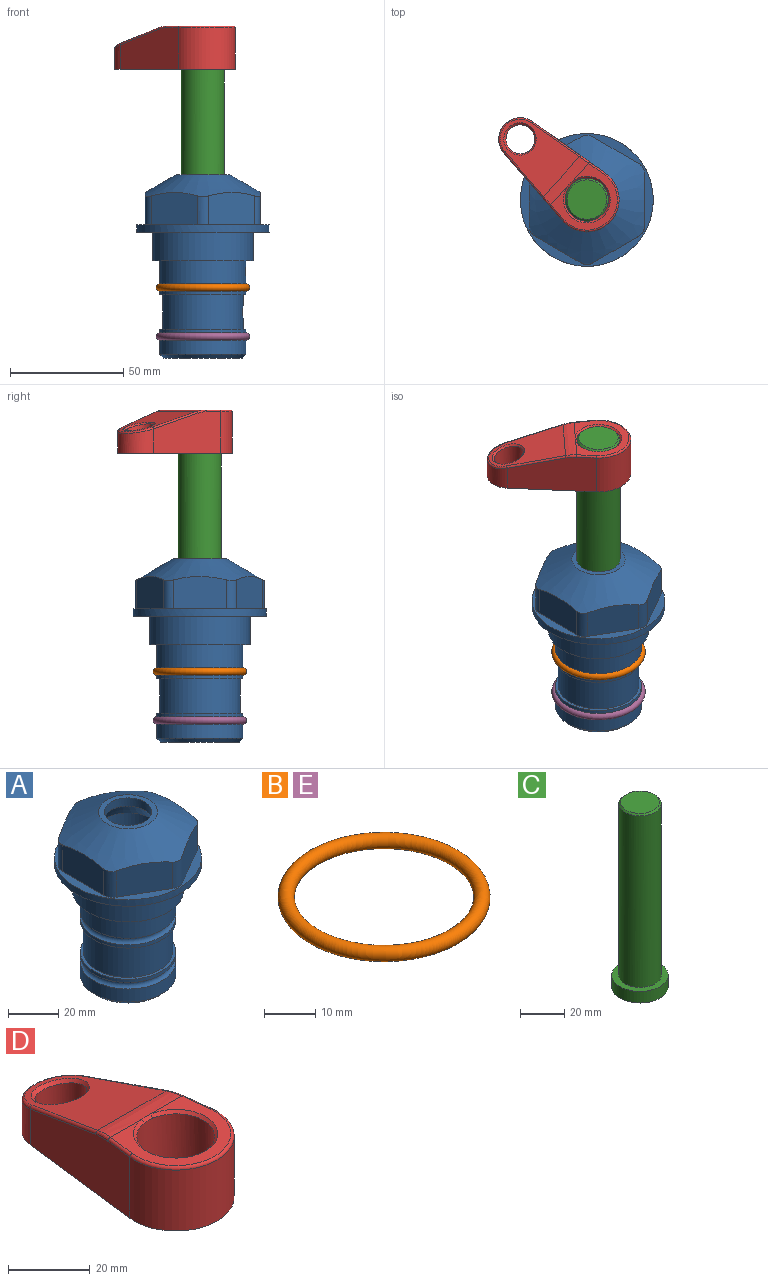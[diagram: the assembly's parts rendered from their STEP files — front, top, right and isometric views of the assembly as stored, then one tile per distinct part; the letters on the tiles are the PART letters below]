
ASSEMBLY  parts=5 mates=4
PART A: 36 faces, bbox 58.7x58.7x81 mm
  f0: cylinder r=17.78mm len=35.56mm, axis (0,0,1), area 1670.8mm2, adj f23,f24,f31
  f1: cylinder r=19.05mm len=38.1mm, axis (0,0,1), area 1191.9mm2, adj f26,f27,f30
  f2: plane 58.66x58.66mm, normal (0,0,-1), area 1150.6mm2, adj f3,f28
  f3: cylinder r=29.33mm len=58.66mm, axis (0,0,-1), area 585.1mm2, adj f2,f4
  f4: plane 58.66x58.66mm, normal (0,0,1), area 475.9mm2, adj f3,f5,f6,f7,f8,f9,f10,f11
  f5: plane 20.32x14.34mm, normal (-0.5,0.87,0), area 324.4mm2, adj f4,f15,f16,f17
  f6: plane 20.32x14.34mm, normal (0.5,0.87,0), area 324.4mm2, adj f4,f14,f15,f17
  f7: plane 23.48x14.34mm, normal (1,0,0), area 324.4mm2, adj f4,f13,f14,f17
  f8: plane 20.32x14.34mm, normal (0.5,-0.87,0), area 324.4mm2, adj f4,f12,f13,f17
  f9: plane 20.32x14.34mm, normal (-0.5,-0.87,0), area 324.4mm2, adj f4,f11,f12,f17
  f10: plane 23.48x14.34mm, normal (-1,0,0), area 324.4mm2, adj f4,f11,f16,f17
  f11: cylinder r=5.08mm len=12.85mm, axis (0,0,-1), area 67.2mm2, adj f4,f9,f10,f17
  f12: cylinder r=5.08mm len=12.85mm, axis (0,0,-1), area 67.2mm2, adj f4,f8,f9,f17
  f13: cylinder r=5.08mm len=12.85mm, axis (0,0,-1), area 67.2mm2, adj f4,f7,f8,f17
  f14: cylinder r=5.08mm len=12.85mm, axis (0,0,-1), area 67.2mm2, adj f4,f6,f7,f17
  f15: cylinder r=5.08mm len=12.85mm, axis (0,0,-1), area 67.2mm2, adj f4,f5,f6,f17
  f16: cylinder r=5.08mm len=12.85mm, axis (0,0,-1), area 67.2mm2, adj f4,f5,f10,f17
  f17: cone r=11.73mm half-angle=60deg, axis (0,0,-1), area 2071.8mm2, adj f5,f6,f7,f8,f9,f10,f11,f12
  f18: plane 23.46x23.46mm, normal (0,0,1), area 147.4mm2, adj f17,f35
  f19: plane 34.93x34.93mm, normal (0,0,-1), area 958mm2, adj f29
  f20: cylinder r=19.05mm len=38.1mm, axis (0,0,1), area 760.1mm2, adj f21,f29
  f21: torus R=19.05mm, axis (0,0,1), area 565.3mm2, adj f20,f22
  f22: cylinder r=19.05mm len=38.1mm, axis (0,0,1), area 190mm2, adj f21,f23
  f23: plane 38.1x38.1mm, normal (0,0,1), area 146.9mm2, adj f0,f22
  f24: plane 38.1x38.1mm, normal (0,0,-1), area 146.9mm2, adj f0,f25
  f25: cylinder r=19.05mm len=38.1mm, axis (0,0,1), area 190mm2, adj f24,f26
  f26: torus R=19.05mm, axis (0,0,1), area 565.3mm2, adj f1,f25
  f27: plane 44.45x44.45mm, normal (0,0,-1), area 411.7mm2, adj f1,f28
  f28: cylinder r=22.23mm len=44.45mm, axis (0,0,1), area 1773.5mm2, adj f2,f27
  f29: cone r=19.05mm half-angle=45deg, axis (0,0,1), area 257.5mm2, adj f19,f20
  f30: cylinder r=3.17mm len=6.75mm, axis (-1,0,0), area 128mm2, adj f1,f33
  f31: cylinder r=3.17mm len=6.35mm, axis (-1,0,0), area 102.5mm2, adj f0,f33
  f32: plane 25.4x25.4mm, normal (0,0,1), area 506.7mm2, adj f33
  f33: cylinder r=12.7mm len=66.42mm, axis (0,0,-1), area 5236.2mm2, adj f30,f31,f32,f34
  f34: cone r=9.53mm half-angle=30deg, axis (0,0,-1), area 443.4mm2, adj f33,f35
  f35: cylinder r=9.53mm len=19.05mm, axis (0,0,-1), area 240.9mm2, adj f18,f34
PART B: 1 faces, bbox 44.7x44.7x3.2 mm
  f0: torus R=19.05mm, axis (0,0,1), area 1193.9mm2
PART C: 6 faces, bbox 25.4x25.4x101.6 mm
  f0: plane 17.46x17.46mm, normal (0,0,1), area 239.5mm2, adj f5
  f1: plane 25.4x25.4mm, normal (0,0,-1), area 506.7mm2, adj f2
  f2: cylinder r=12.7mm len=25.4mm, axis (0,0,1), area 506.7mm2, adj f1,f3
  f3: plane 25.4x25.4mm, normal (0,0,1), area 221.7mm2, adj f2,f4
  f4: cylinder r=9.53mm len=94.46mm, axis (0,0,1), area 5653mm2, adj f3,f5
  f5: cone r=8.73mm half-angle=45deg, axis (0,0,-1), area 64.4mm2, adj f0,f4
PART D: 31 faces, bbox 31.7x65.5x19.8 mm
  f0: plane 39.12x18.26mm, normal (0.99,0.12,0), area 612.2mm2, adj f1,f4,f7,f11,f13,f15
  f1: cylinder r=9.53mm len=18.91mm, axis (0,0,-1), area 296.1mm2, adj f0,f2,f7,f17
  f2: plane 39.12x18.26mm, normal (-0.99,0.12,0), area 612.2mm2, adj f1,f4,f7,f12,f14,f16
  f3: cylinder r=6.35mm len=12.7mm, axis (0,0,-1), area 362.4mm2, adj f7,f18
  f4: cylinder r=14.29mm len=28.58mm, axis (0,0,-1), area 882.2mm2, adj f0,f2,f7,f10
  f5: cylinder r=9.53mm len=19.05mm, axis (0,0,-1), area 1092.6mm2, adj f7,f19,f20
  f6: plane 26.99x23.69mm, normal (0,0,1), area 216.2mm2, adj f9,f10,f11,f12,f19
  f7: plane 63.5x28.58mm, normal (0,0,-1), area 661.8mm2, adj f0,f1,f2,f3,f4,f5,f22,f23
  f8: plane 33.52x23.6mm, normal (0,0.26,0.97), area 486mm2, adj f9,f15,f16,f17,f18
  f9: cylinder r=19.05mm len=24.72mm, axis (1,0,0), area 120.4mm2, adj f6,f8,f13,f14,f20
  f10: torus R=13.49mm, axis (0,0,1), area 59mm2, adj f4,f6,f11,f12
  f11: cylinder r=0.79mm len=8.67mm, axis (0.12,-0.99,0), area 10.8mm2, adj f0,f6,f10,f13
  f12: cylinder r=0.79mm len=8.67mm, axis (0.12,0.99,0), area 10.8mm2, adj f2,f6,f10,f14
  f13: bspline ~4.95x1.42mm, area 6.1mm2, adj f0,f9,f11,f15
  f14: bspline ~4.95x1.42mm, area 6.1mm2, adj f2,f9,f12,f16
  f15: cylinder r=0.79mm len=25.95mm, axis (0.12,-0.96,0.26), area 32.9mm2, adj f0,f8,f13,f17
  f16: cylinder r=0.79mm len=25.95mm, axis (0.12,0.96,-0.26), area 32.9mm2, adj f2,f8,f14,f17
  f17: bspline ~18.91x8.38mm, area 30mm2, adj f1,f8,f15,f16
  f18: bspline ~14.29x14.29mm, area 48.3mm2, adj f3,f8
  f19: cone r=9.53mm half-angle=45deg, axis (0,0,1), area 66.5mm2, adj f5,f6,f20
  f20: bspline ~3.22x0.96mm, area 3.5mm2, adj f5,f9,f19
  f21: plane 2.75x2.72mm, normal (0,0,-1), area 2.9mm2, adj f23,f25,f28
  f22: plane 23.05x15.88mm, normal (-0.99,-0.12,0), area 323.6mm2, adj f7,f25,f26,f27,f28,f29
  f23: plane 23.05x15.88mm, normal (0.99,-0.12,0), area 323.6mm2, adj f7,f21,f25,f27,f28,f30
  f24: cylinder r=9.53mm len=10.69mm, axis (0,0,-1), area 114.7mm2, adj f7,f27,f29,f30
  f25: cylinder r=12.7mm len=20.59mm, axis (0,0,-1), area 381.1mm2, adj f7,f21,f22,f23,f26,f28
  f26: plane 2.75x2.72mm, normal (0,0,-1), area 2.9mm2, adj f22,f25,f28
  f27: plane 19.72x18.37mm, normal (0,-0.26,-0.97), area 291.8mm2, adj f22,f23,f24,f28,f29,f30
  f28: cylinder r=15.88mm len=19.92mm, axis (1,0,0), area 54.8mm2, adj f21,f22,f23,f25,f26,f27
  f29: cylinder r=1.59mm len=11mm, axis (0,0,-1), area 34.7mm2, adj f7,f22,f24,f27
  f30: cylinder r=1.59mm len=11mm, axis (0,0,-1), area 34.7mm2, adj f7,f23,f24,f27
PART E: same geometry as B
PLACE A at identity fixed
PLACE B at identity
PLACE C rot(axis=(0,0,1),47.7deg) t=(0,0,27.55)mm
PLACE D rot(axis=(0,0,1),47.7deg) t=(0,0,27.55)mm
PLACE E t=(0,0,-21.59)mm
MATE fastened A.f0 <-> E.f0  axis (0,0,1) through (0,0,-46.1)mm
MATE fastened A.f0 <-> B.f0  axis (0,0,1) through (0,0,-24.51)mm
MATE cylindrical A.f0 <-> C.f2  axis (0,0,1) through (0,0,-50.55)mm
MATE fastened C.f2 <-> D.f4  axis (0,0,1) through (0,0,91.05)mm
